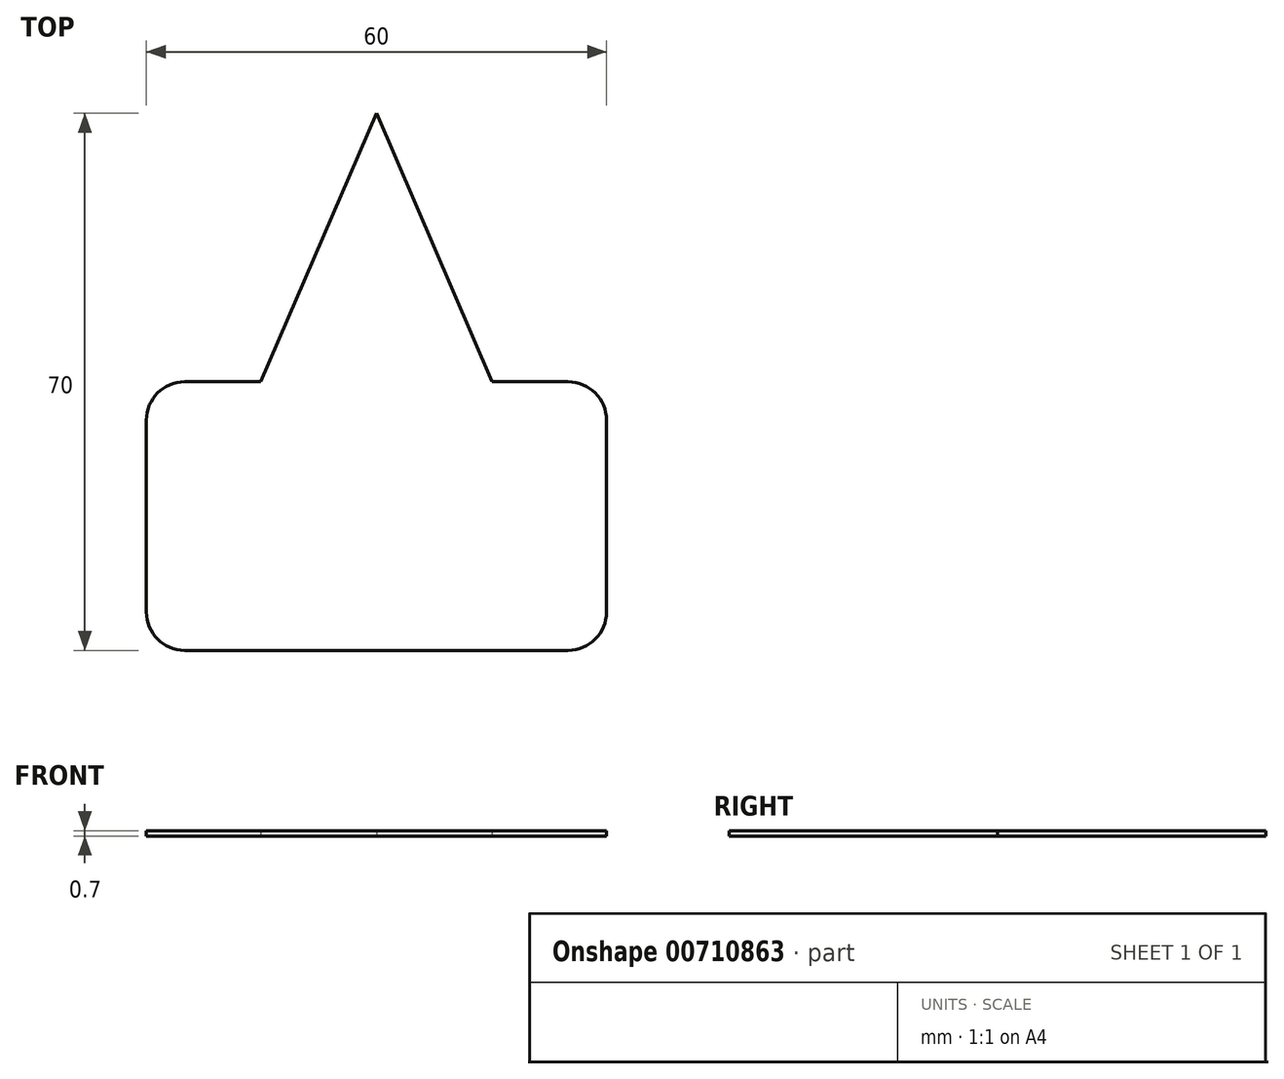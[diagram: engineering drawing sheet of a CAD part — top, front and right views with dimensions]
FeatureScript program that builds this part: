
annotation { "Feature Type Name" : "Feature", "Feature Type Description" : "" }
export const myFeature = defineFeature(function(context is Context, id is Id, definition is map)
    precondition{}
    {
        {
            var Q0;
            Q0=qCreatedBy(makeId("Top.planeOp"),FACE);
            var sketch = newSketch(context, id + "F0", { "sketchPlane" : qUnion([Q0])});
            skLineSegment(sketch, "E0", {"start": v(0, 0) * mm, "end": v(0, 120.85) * mm, "construction": true});
            skLineSegment(sketch, "E1", {"start": v(0, 0) * mm, "end": v(-25, 0) * mm});
            skLineSegment(sketch, "E2", {"start": v(-30, 5) * mm, "end": v(-30, 30) * mm});
            skLineSegment(sketch, "E3", {"start": v(-25, 35) * mm, "end": v(-15.1, 35) * mm});
            skPoint(sketch, "E4.visualSharp", {"position": v(-30, 35) * mm});
            skArc(sketch, "E4.filletArc", {"start": v(-25, 35) * mm, "mid": v(-28.54, 33.54) * mm, "end": v(-30, 30) * mm});
            skPoint(sketch, "E5.visualSharp", {"position": v(-30, 0) * mm});
            skArc(sketch, "E5.filletArc", {"start": v(-30, 5) * mm, "mid": v(-28.54, 1.46) * mm, "end": v(-25, 0) * mm});
            skLineSegment(sketch, "E6", {"start": v(-15.1, 35) * mm, "end": v(0, 70) * mm});
            skLineSegment(sketch, "E7.MirrorCS", {"start": v(15.1, 35) * mm, "end": v(0, 70) * mm});
            skLineSegment(sketch, "E8.MirrorCS", {"start": v(25, 35) * mm, "end": v(15.1, 35) * mm});
            skArc(sketch, "E9.MirrorCS", {"start": v(25, 35) * mm, "mid": v(28.54, 33.54) * mm, "end": v(30, 30) * mm});
            skLineSegment(sketch, "E10.MirrorCS", {"start": v(30, 5) * mm, "end": v(30, 30) * mm});
            skArc(sketch, "E11.MirrorCS", {"start": v(30, 5) * mm, "mid": v(28.54, 1.46) * mm, "end": v(25, 0) * mm});
            skLineSegment(sketch, "E12.MirrorCS", {"start": v(0, 0) * mm, "end": v(25, 0) * mm});
            skPoint(sketch, "E13.orphan", {"position": v(0, 35) * mm});
            skLineSegment(sketch, "E14", {"start": v(-15.1, 35) * mm, "end": v(15.1, 35) * mm, "construction": true});
            skSolve(sketch);
        }
        {
            var Q0;
            Q0 = qSketchRegion(id + "F0", true);
            extrude(context, id + "F1", {"entities" : qUnion([Q0]), "depth" : 0.7 * mm, "offsetDistance" : 25 * mm});
        }
    });
